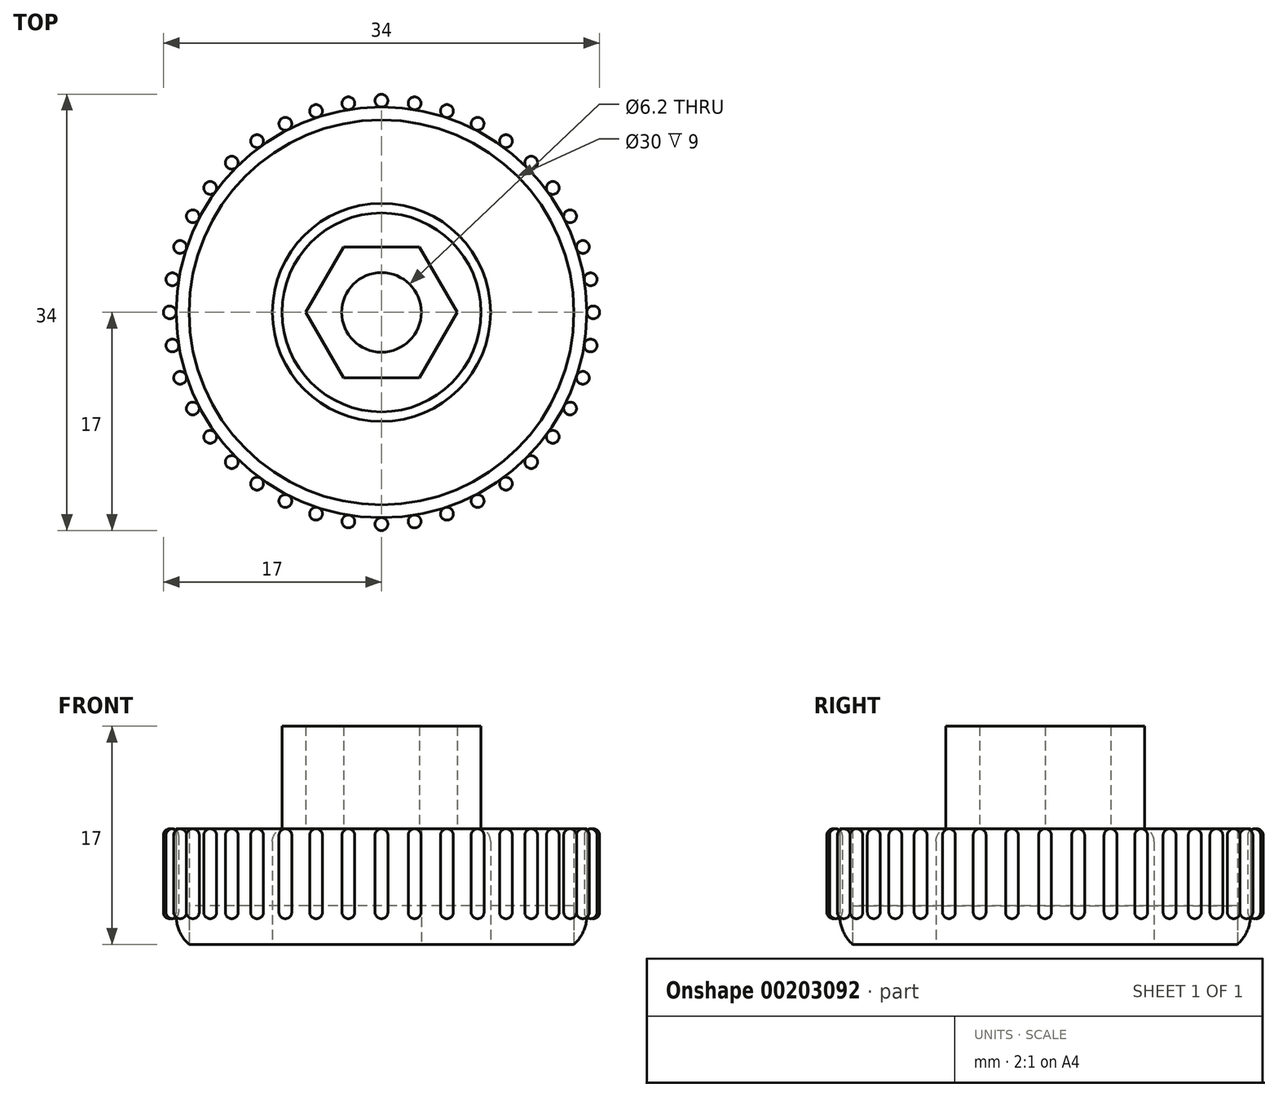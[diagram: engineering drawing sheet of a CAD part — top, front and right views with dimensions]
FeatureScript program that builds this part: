
annotation { "Feature Type Name" : "Feature", "Feature Type Description" : "" }
export const myFeature = defineFeature(function(context is Context, id is Id, definition is map)
    precondition{}
    {
        {
            var Q0;
            Q0=qCreatedBy(makeId("Top.planeOp"),FACE);
            var sketch = newSketch(context, id + "F0", { "sketchPlane" : qUnion([Q0])});
            skCircle(sketch, "E0.cCircle", {"center": v(0, 0) * mm, "radius": 5.9 * mm, "construction": true});
            skLineSegment(sketch, "E0.0", {"start": v(5.9, 0) * mm, "end": v(2.95, -5.1) * mm});
            skLineSegment(sketch, "E0.1", {"start": v(2.95, -5.1) * mm, "end": v(-2.95, -5.1) * mm});
            skLineSegment(sketch, "E0.2", {"start": v(-2.95, -5.1) * mm, "end": v(-5.9, 0) * mm});
            skLineSegment(sketch, "E0.3", {"start": v(-5.9, 0) * mm, "end": v(-2.95, 5.1) * mm});
            skLineSegment(sketch, "E0.4", {"start": v(-2.95, 5.1) * mm, "end": v(2.95, 5.1) * mm});
            skLineSegment(sketch, "E0.5", {"start": v(2.95, 5.1) * mm, "end": v(5.9, 0) * mm});
            skCircle(sketch, "E1", {"center": v(0, 0) * mm, "radius": 7.75 * mm});
            skCircle(sketch, "E2", {"center": v(0, 0) * mm, "radius": 8.5 * mm});
            skCircle(sketch, "E3", {"center": v(0, 0) * mm, "radius": 16 * mm});
            skCircle(sketch, "E4", {"center": v(0, 0) * mm, "radius": 15 * mm});
            skCircle(sketch, "E5", {"center": v(0, 0) * mm, "radius": 3.1 * mm});
            skSolve(sketch);
        }
        {
            var Q0;
            Q0=qCreatedBy(makeId("Top.planeOp"),FACE);
            var sketch = newSketch(context, id + "F1", { "sketchPlane" : qUnion([Q0])});
            skCircle(sketch, "E6", {"center": v(0, 16.5) * mm, "radius": 0.5 * mm});
            skCircle(sketch, "E7.1.0", {"center": v(-2.58, 16.3) * mm, "radius": 0.5 * mm});
            skCircle(sketch, "E7.2.0", {"center": v(-5.1, 15.7) * mm, "radius": 0.5 * mm});
            skCircle(sketch, "E7.3.0", {"center": v(-7.5, 14.7) * mm, "radius": 0.5 * mm});
            skCircle(sketch, "E7.4.0", {"center": v(-9.7, 13.35) * mm, "radius": 0.5 * mm});
            skCircle(sketch, "E7.5.0", {"center": v(-11.67, 11.67) * mm, "radius": 0.5 * mm});
            skCircle(sketch, "E7.6.0", {"center": v(-13.35, 9.7) * mm, "radius": 0.5 * mm});
            skCircle(sketch, "E7.7.0", {"center": v(-14.7, 7.5) * mm, "radius": 0.5 * mm});
            skCircle(sketch, "E7.8.0", {"center": v(-15.7, 5.1) * mm, "radius": 0.5 * mm});
            skCircle(sketch, "E7.9.0", {"center": v(-16.3, 2.58) * mm, "radius": 0.5 * mm});
            skCircle(sketch, "E7.10.0", {"center": v(-16.5, 0) * mm, "radius": 0.5 * mm});
            skCircle(sketch, "E7.11.0", {"center": v(-16.3, -2.58) * mm, "radius": 0.5 * mm});
            skCircle(sketch, "E7.12.0", {"center": v(-15.7, -5.1) * mm, "radius": 0.5 * mm});
            skCircle(sketch, "E7.13.0", {"center": v(-14.7, -7.5) * mm, "radius": 0.5 * mm});
            skCircle(sketch, "E7.14.0", {"center": v(-13.35, -9.7) * mm, "radius": 0.5 * mm});
            skCircle(sketch, "E7.15.0", {"center": v(-11.67, -11.67) * mm, "radius": 0.5 * mm});
            skCircle(sketch, "E7.16.0", {"center": v(-9.7, -13.35) * mm, "radius": 0.5 * mm});
            skCircle(sketch, "E7.17.0", {"center": v(-7.5, -14.7) * mm, "radius": 0.5 * mm});
            skCircle(sketch, "E7.18.0", {"center": v(-5.1, -15.7) * mm, "radius": 0.5 * mm});
            skCircle(sketch, "E7.19.0", {"center": v(-2.58, -16.3) * mm, "radius": 0.5 * mm});
            skCircle(sketch, "E7.20.0", {"center": v(0, -16.5) * mm, "radius": 0.5 * mm});
            skCircle(sketch, "E7.21.0", {"center": v(2.58, -16.3) * mm, "radius": 0.5 * mm});
            skCircle(sketch, "E7.22.0", {"center": v(5.1, -15.7) * mm, "radius": 0.5 * mm});
            skCircle(sketch, "E7.23.0", {"center": v(7.5, -14.7) * mm, "radius": 0.5 * mm});
            skCircle(sketch, "E7.24.0", {"center": v(9.7, -13.35) * mm, "radius": 0.5 * mm});
            skCircle(sketch, "E7.25.0", {"center": v(11.67, -11.67) * mm, "radius": 0.5 * mm});
            skCircle(sketch, "E7.26.0", {"center": v(13.35, -9.7) * mm, "radius": 0.5 * mm});
            skCircle(sketch, "E7.27.0", {"center": v(14.7, -7.5) * mm, "radius": 0.5 * mm});
            skCircle(sketch, "E7.28.0", {"center": v(15.7, -5.1) * mm, "radius": 0.5 * mm});
            skCircle(sketch, "E7.29.0", {"center": v(16.3, -2.58) * mm, "radius": 0.5 * mm});
            skCircle(sketch, "E7.30.0", {"center": v(16.5, 0) * mm, "radius": 0.5 * mm});
            skCircle(sketch, "E7.31.0", {"center": v(16.3, 2.58) * mm, "radius": 0.5 * mm});
            skCircle(sketch, "E7.32.0", {"center": v(15.7, 5.1) * mm, "radius": 0.5 * mm});
            skCircle(sketch, "E7.33.0", {"center": v(14.7, 7.5) * mm, "radius": 0.5 * mm});
            skCircle(sketch, "E7.34.0", {"center": v(13.35, 9.7) * mm, "radius": 0.5 * mm});
            skCircle(sketch, "E7.35.0", {"center": v(11.67, 11.67) * mm, "radius": 0.5 * mm});
            skCircle(sketch, "E7.36.0", {"center": v(9.7, 13.35) * mm, "radius": 0.5 * mm});
            skCircle(sketch, "E7.37.0", {"center": v(7.5, 14.7) * mm, "radius": 0.5 * mm});
            skCircle(sketch, "E7.38.0", {"center": v(5.1, 15.7) * mm, "radius": 0.5 * mm});
            skCircle(sketch, "E7.39.0", {"center": v(2.58, 16.3) * mm, "radius": 0.5 * mm});
            skPoint(sketch, "E7.center", {"position": v(0, 0) * mm});
            skSolve(sketch);
        }
        {
            var Q0;
            Q0=makeQuery(id+"F1.imprint","IMPRINT",FACE,{"disambiguationData":[TD([[makeQuery(id+"F1.imprint","IMPRINT",EDGE,{"derivedFrom":sQuery(id+"F1.wireOp",EDGE,"E6")}),1.0]])]});
            var Q1;
            Q1=makeQuery(id+"F1.imprint","IMPRINT",FACE,{"disambiguationData":[TD([[makeQuery(id+"F1.imprint","IMPRINT",EDGE,{"derivedFrom":sQuery(id+"F1.wireOp",EDGE,"E7.39.0")}),1.0]])]});
            var Q2;
            Q2=makeQuery(id+"F1.imprint","IMPRINT",FACE,{"disambiguationData":[TD([[makeQuery(id+"F1.imprint","IMPRINT",EDGE,{"derivedFrom":sQuery(id+"F1.wireOp",EDGE,"E7.38.0")}),1.0]])]});
            var Q3;
            Q3=makeQuery(id+"F1.imprint","IMPRINT",FACE,{"disambiguationData":[TD([[makeQuery(id+"F1.imprint","IMPRINT",EDGE,{"derivedFrom":sQuery(id+"F1.wireOp",EDGE,"E7.37.0")}),1.0]])]});
            var Q4;
            Q4=makeQuery(id+"F1.imprint","IMPRINT",FACE,{"disambiguationData":[TD([[makeQuery(id+"F1.imprint","IMPRINT",EDGE,{"derivedFrom":sQuery(id+"F1.wireOp",EDGE,"E7.36.0")}),1.0]])]});
            var Q5;
            Q5=makeQuery(id+"F1.imprint","IMPRINT",FACE,{"disambiguationData":[TD([[makeQuery(id+"F1.imprint","IMPRINT",EDGE,{"derivedFrom":sQuery(id+"F1.wireOp",EDGE,"E7.35.0")}),1.0]])]});
            var Q6;
            Q6=makeQuery(id+"F1.imprint","IMPRINT",FACE,{"disambiguationData":[TD([[makeQuery(id+"F1.imprint","IMPRINT",EDGE,{"derivedFrom":sQuery(id+"F1.wireOp",EDGE,"E7.1.0")}),1.0]])]});
            var Q7;
            Q7=makeQuery(id+"F1.imprint","IMPRINT",FACE,{"disambiguationData":[TD([[makeQuery(id+"F1.imprint","IMPRINT",EDGE,{"derivedFrom":sQuery(id+"F1.wireOp",EDGE,"E7.2.0")}),1.0]])]});
            var Q8;
            Q8=makeQuery(id+"F1.imprint","IMPRINT",FACE,{"disambiguationData":[TD([[makeQuery(id+"F1.imprint","IMPRINT",EDGE,{"derivedFrom":sQuery(id+"F1.wireOp",EDGE,"E7.3.0")}),1.0]])]});
            var Q9;
            Q9=makeQuery(id+"F1.imprint","IMPRINT",FACE,{"disambiguationData":[TD([[makeQuery(id+"F1.imprint","IMPRINT",EDGE,{"derivedFrom":sQuery(id+"F1.wireOp",EDGE,"E7.4.0")}),1.0]])]});
            var Q10;
            Q10=makeQuery(id+"F1.imprint","IMPRINT",FACE,{"disambiguationData":[TD([[makeQuery(id+"F1.imprint","IMPRINT",EDGE,{"derivedFrom":sQuery(id+"F1.wireOp",EDGE,"E7.5.0")}),1.0]])]});
            var Q11;
            Q11=makeQuery(id+"F1.imprint","IMPRINT",FACE,{"disambiguationData":[TD([[makeQuery(id+"F1.imprint","IMPRINT",EDGE,{"derivedFrom":sQuery(id+"F1.wireOp",EDGE,"E7.6.0")}),1.0]])]});
            var Q12;
            Q12=makeQuery(id+"F1.imprint","IMPRINT",FACE,{"disambiguationData":[TD([[makeQuery(id+"F1.imprint","IMPRINT",EDGE,{"derivedFrom":sQuery(id+"F1.wireOp",EDGE,"E7.7.0")}),1.0]])]});
            var Q13;
            Q13=makeQuery(id+"F1.imprint","IMPRINT",FACE,{"disambiguationData":[TD([[makeQuery(id+"F1.imprint","IMPRINT",EDGE,{"derivedFrom":sQuery(id+"F1.wireOp",EDGE,"E7.8.0")}),1.0]])]});
            var Q14;
            Q14=makeQuery(id+"F1.imprint","IMPRINT",FACE,{"disambiguationData":[TD([[makeQuery(id+"F1.imprint","IMPRINT",EDGE,{"derivedFrom":sQuery(id+"F1.wireOp",EDGE,"E7.9.0")}),1.0]])]});
            var Q15;
            Q15=makeQuery(id+"F1.imprint","IMPRINT",FACE,{"disambiguationData":[TD([[makeQuery(id+"F1.imprint","IMPRINT",EDGE,{"derivedFrom":sQuery(id+"F1.wireOp",EDGE,"E7.10.0")}),1.0]])]});
            var Q16;
            Q16=makeQuery(id+"F1.imprint","IMPRINT",FACE,{"disambiguationData":[TD([[makeQuery(id+"F1.imprint","IMPRINT",EDGE,{"derivedFrom":sQuery(id+"F1.wireOp",EDGE,"E7.11.0")}),1.0]])]});
            var Q17;
            Q17=makeQuery(id+"F1.imprint","IMPRINT",FACE,{"disambiguationData":[TD([[makeQuery(id+"F1.imprint","IMPRINT",EDGE,{"derivedFrom":sQuery(id+"F1.wireOp",EDGE,"E7.12.0")}),1.0]])]});
            var Q18;
            Q18=makeQuery(id+"F1.imprint","IMPRINT",FACE,{"disambiguationData":[TD([[makeQuery(id+"F1.imprint","IMPRINT",EDGE,{"derivedFrom":sQuery(id+"F1.wireOp",EDGE,"E7.13.0")}),1.0]])]});
            var Q19;
            Q19=makeQuery(id+"F1.imprint","IMPRINT",FACE,{"disambiguationData":[TD([[makeQuery(id+"F1.imprint","IMPRINT",EDGE,{"derivedFrom":sQuery(id+"F1.wireOp",EDGE,"E7.14.0")}),1.0]])]});
            var Q20;
            Q20=makeQuery(id+"F1.imprint","IMPRINT",FACE,{"disambiguationData":[TD([[makeQuery(id+"F1.imprint","IMPRINT",EDGE,{"derivedFrom":sQuery(id+"F1.wireOp",EDGE,"E7.15.0")}),1.0]])]});
            var Q21;
            Q21=makeQuery(id+"F1.imprint","IMPRINT",FACE,{"disambiguationData":[TD([[makeQuery(id+"F1.imprint","IMPRINT",EDGE,{"derivedFrom":sQuery(id+"F1.wireOp",EDGE,"E7.16.0")}),1.0]])]});
            var Q22;
            Q22=makeQuery(id+"F1.imprint","IMPRINT",FACE,{"disambiguationData":[TD([[makeQuery(id+"F1.imprint","IMPRINT",EDGE,{"derivedFrom":sQuery(id+"F1.wireOp",EDGE,"E7.17.0")}),1.0]])]});
            var Q23;
            Q23=makeQuery(id+"F1.imprint","IMPRINT",FACE,{"disambiguationData":[TD([[makeQuery(id+"F1.imprint","IMPRINT",EDGE,{"derivedFrom":sQuery(id+"F1.wireOp",EDGE,"E7.18.0")}),1.0]])]});
            var Q24;
            Q24=makeQuery(id+"F1.imprint","IMPRINT",FACE,{"disambiguationData":[TD([[makeQuery(id+"F1.imprint","IMPRINT",EDGE,{"derivedFrom":sQuery(id+"F1.wireOp",EDGE,"E7.19.0")}),1.0]])]});
            var Q25;
            Q25=makeQuery(id+"F1.imprint","IMPRINT",FACE,{"disambiguationData":[TD([[makeQuery(id+"F1.imprint","IMPRINT",EDGE,{"derivedFrom":sQuery(id+"F1.wireOp",EDGE,"E7.20.0")}),1.0]])]});
            var Q26;
            Q26=makeQuery(id+"F1.imprint","IMPRINT",FACE,{"disambiguationData":[TD([[makeQuery(id+"F1.imprint","IMPRINT",EDGE,{"derivedFrom":sQuery(id+"F1.wireOp",EDGE,"E7.21.0")}),1.0]])]});
            var Q27;
            Q27=makeQuery(id+"F1.imprint","IMPRINT",FACE,{"disambiguationData":[TD([[makeQuery(id+"F1.imprint","IMPRINT",EDGE,{"derivedFrom":sQuery(id+"F1.wireOp",EDGE,"E7.22.0")}),1.0]])]});
            var Q28;
            Q28=makeQuery(id+"F1.imprint","IMPRINT",FACE,{"disambiguationData":[TD([[makeQuery(id+"F1.imprint","IMPRINT",EDGE,{"derivedFrom":sQuery(id+"F1.wireOp",EDGE,"E7.23.0")}),1.0]])]});
            var Q29;
            Q29=makeQuery(id+"F1.imprint","IMPRINT",FACE,{"disambiguationData":[TD([[makeQuery(id+"F1.imprint","IMPRINT",EDGE,{"derivedFrom":sQuery(id+"F1.wireOp",EDGE,"E7.24.0")}),1.0]])]});
            var Q30;
            Q30=makeQuery(id+"F1.imprint","IMPRINT",FACE,{"disambiguationData":[TD([[makeQuery(id+"F1.imprint","IMPRINT",EDGE,{"derivedFrom":sQuery(id+"F1.wireOp",EDGE,"E7.25.0")}),1.0]])]});
            var Q31;
            Q31=makeQuery(id+"F1.imprint","IMPRINT",FACE,{"disambiguationData":[TD([[makeQuery(id+"F1.imprint","IMPRINT",EDGE,{"derivedFrom":sQuery(id+"F1.wireOp",EDGE,"E7.26.0")}),1.0]])]});
            var Q32;
            Q32=makeQuery(id+"F1.imprint","IMPRINT",FACE,{"disambiguationData":[TD([[makeQuery(id+"F1.imprint","IMPRINT",EDGE,{"derivedFrom":sQuery(id+"F1.wireOp",EDGE,"E7.27.0")}),1.0]])]});
            var Q33;
            Q33=makeQuery(id+"F1.imprint","IMPRINT",FACE,{"disambiguationData":[TD([[makeQuery(id+"F1.imprint","IMPRINT",EDGE,{"derivedFrom":sQuery(id+"F1.wireOp",EDGE,"E7.28.0")}),1.0]])]});
            var Q34;
            Q34=makeQuery(id+"F1.imprint","IMPRINT",FACE,{"disambiguationData":[TD([[makeQuery(id+"F1.imprint","IMPRINT",EDGE,{"derivedFrom":sQuery(id+"F1.wireOp",EDGE,"E7.29.0")}),1.0]])]});
            var Q35;
            Q35=makeQuery(id+"F1.imprint","IMPRINT",FACE,{"disambiguationData":[TD([[makeQuery(id+"F1.imprint","IMPRINT",EDGE,{"derivedFrom":sQuery(id+"F1.wireOp",EDGE,"E7.34.0")}),1.0]])]});
            var Q36;
            Q36=makeQuery(id+"F1.imprint","IMPRINT",FACE,{"disambiguationData":[TD([[makeQuery(id+"F1.imprint","IMPRINT",EDGE,{"derivedFrom":sQuery(id+"F1.wireOp",EDGE,"E7.33.0")}),1.0]])]});
            var Q37;
            Q37=makeQuery(id+"F1.imprint","IMPRINT",FACE,{"disambiguationData":[TD([[makeQuery(id+"F1.imprint","IMPRINT",EDGE,{"derivedFrom":sQuery(id+"F1.wireOp",EDGE,"E7.32.0")}),1.0]])]});
            var Q38;
            Q38=makeQuery(id+"F1.imprint","IMPRINT",FACE,{"disambiguationData":[TD([[makeQuery(id+"F1.imprint","IMPRINT",EDGE,{"derivedFrom":sQuery(id+"F1.wireOp",EDGE,"E7.31.0")}),1.0]])]});
            var Q39;
            Q39=makeQuery(id+"F1.imprint","IMPRINT",FACE,{"disambiguationData":[TD([[makeQuery(id+"F1.imprint","IMPRINT",EDGE,{"derivedFrom":sQuery(id+"F1.wireOp",EDGE,"E7.30.0")}),1.0]])]});
            extrude(context, id + "F2", {"entities" : qUnion([Q0, Q1, Q2, Q3, Q4, Q5, Q6, Q7, Q8, Q9, Q10, Q11, Q12, Q13, Q14, Q15, Q16, Q17, Q18, Q19, Q20, Q21, Q22, Q23, Q24, Q25, Q26, Q27, Q28, Q29, Q30, Q31, Q32, Q33, Q34, Q35, Q36, Q37, Q38, Q39]), "depth" : 7 * mm});
        }
        {
            var Q0;
            Q0=makeQuery(id+"F0.imprint","IMPRINT",FACE,{"disambiguationData":[TD([[makeQuery(id+"F0.imprint","IMPRINT",EDGE,{"derivedFrom":sQuery(id+"F0.wireOp",EDGE,"E3")}),1.0]])]});
            var Q1;
            Q1=makeQuery(id+"F0.imprint","IMPRINT",FACE,{"disambiguationData":[TD([[makeQuery(id+"F0.imprint","IMPRINT",EDGE,{"derivedFrom":sQuery(id+"F0.wireOp",EDGE,"E1")}),-1.0]])]});
            var Q2;
            Q2=makeQuery(id+"F0.imprint","IMPRINT",FACE,{"disambiguationData":[TD([[makeQuery(id+"F0.imprint","IMPRINT",EDGE,{"derivedFrom":sQuery(id+"F0.wireOp",EDGE,"E0.0")}),-1.0]])]});
            extrude(context, id + "F3", {"entities" : qUnion([Q0, Q1, Q2]), "depth" : 9 * mm});
        }
        {
            var Q0;
            Q0=makeQuery(id+"F0.imprint","IMPRINT",FACE,{"disambiguationData":[TD([[makeQuery(id+"F0.imprint","IMPRINT",EDGE,{"derivedFrom":sQuery(id+"F0.wireOp",EDGE,"E0.0")}),1.0]])]});
            extrude(context, id + "F4", {"entities" : qUnion([Q0]), "operationType" : NewBodyOperationType.ADD, "depth" : 17 * mm});
        }
        {
            var Q0;
            Q0=makeQuery(id+"F2.opExtrude","SWEPT_BODY",BODY,{"disambiguationData":[OSD([sQuery(id+"F1.wireOp",EDGE,"E7.3.0")])]});
            var Q1;
            Q1=makeQuery(id+"F2.opExtrude","SWEPT_BODY",BODY,{"disambiguationData":[OSD([sQuery(id+"F1.wireOp",EDGE,"E7.2.0")])]});
            var Q2;
            Q2=makeQuery(id+"F2.opExtrude","SWEPT_BODY",BODY,{"disambiguationData":[OSD([sQuery(id+"F1.wireOp",EDGE,"E7.1.0")])]});
            var Q3;
            Q3=makeQuery(id+"F2.opExtrude","SWEPT_BODY",BODY,{"disambiguationData":[OSD([sQuery(id+"F1.wireOp",EDGE,"E6")])]});
            var Q4;
            Q4=makeQuery(id+"F2.opExtrude","SWEPT_BODY",BODY,{"disambiguationData":[OSD([sQuery(id+"F1.wireOp",EDGE,"E7.39.0")])]});
            var Q5;
            Q5=makeQuery(id+"F2.opExtrude","SWEPT_BODY",BODY,{"disambiguationData":[OSD([sQuery(id+"F1.wireOp",EDGE,"E7.38.0")])]});
            var Q6;
            Q6=makeQuery(id+"F2.opExtrude","SWEPT_BODY",BODY,{"disambiguationData":[OSD([sQuery(id+"F1.wireOp",EDGE,"E7.37.0")])]});
            var Q7;
            Q7=makeQuery(id+"F2.opExtrude","SWEPT_BODY",BODY,{"disambiguationData":[OSD([sQuery(id+"F1.wireOp",EDGE,"E7.36.0")])]});
            var Q8;
            Q8=makeQuery(id+"F2.opExtrude","SWEPT_BODY",BODY,{"disambiguationData":[OSD([sQuery(id+"F1.wireOp",EDGE,"E7.35.0")])]});
            var Q9;
            Q9=makeQuery(id+"F2.opExtrude","SWEPT_BODY",BODY,{"disambiguationData":[OSD([sQuery(id+"F1.wireOp",EDGE,"E7.34.0")])]});
            var Q10;
            Q10=makeQuery(id+"F2.opExtrude","SWEPT_BODY",BODY,{"disambiguationData":[OSD([sQuery(id+"F1.wireOp",EDGE,"E7.33.0")])]});
            var Q11;
            Q11=makeQuery(id+"F2.opExtrude","SWEPT_BODY",BODY,{"disambiguationData":[OSD([sQuery(id+"F1.wireOp",EDGE,"E7.4.0")])]});
            var Q12;
            Q12=makeQuery(id+"F2.opExtrude","SWEPT_BODY",BODY,{"disambiguationData":[OSD([sQuery(id+"F1.wireOp",EDGE,"E7.5.0")])]});
            var Q13;
            Q13=makeQuery(id+"F2.opExtrude","SWEPT_BODY",BODY,{"disambiguationData":[OSD([sQuery(id+"F1.wireOp",EDGE,"E7.6.0")])]});
            var Q14;
            Q14=makeQuery(id+"F2.opExtrude","SWEPT_BODY",BODY,{"disambiguationData":[OSD([sQuery(id+"F1.wireOp",EDGE,"E7.7.0")])]});
            var Q15;
            Q15=makeQuery(id+"F2.opExtrude","SWEPT_BODY",BODY,{"disambiguationData":[OSD([sQuery(id+"F1.wireOp",EDGE,"E7.8.0")])]});
            var Q16;
            Q16=makeQuery(id+"F2.opExtrude","SWEPT_BODY",BODY,{"disambiguationData":[OSD([sQuery(id+"F1.wireOp",EDGE,"E7.9.0")])]});
            var Q17;
            Q17=makeQuery(id+"F2.opExtrude","SWEPT_BODY",BODY,{"disambiguationData":[OSD([sQuery(id+"F1.wireOp",EDGE,"E7.31.0")])]});
            var Q18;
            Q18=makeQuery(id+"F2.opExtrude","SWEPT_BODY",BODY,{"disambiguationData":[OSD([sQuery(id+"F1.wireOp",EDGE,"E7.30.0")])]});
            var Q19;
            Q19=makeQuery(id+"F2.opExtrude","SWEPT_BODY",BODY,{"disambiguationData":[OSD([sQuery(id+"F1.wireOp",EDGE,"E7.28.0")])]});
            var Q20;
            Q20=makeQuery(id+"F2.opExtrude","SWEPT_BODY",BODY,{"disambiguationData":[OSD([sQuery(id+"F1.wireOp",EDGE,"E7.27.0")])]});
            var Q21;
            Q21=makeQuery(id+"F2.opExtrude","SWEPT_BODY",BODY,{"disambiguationData":[OSD([sQuery(id+"F1.wireOp",EDGE,"E7.26.0")])]});
            var Q22;
            Q22=makeQuery(id+"F2.opExtrude","SWEPT_BODY",BODY,{"disambiguationData":[OSD([sQuery(id+"F1.wireOp",EDGE,"E7.25.0")])]});
            var Q23;
            Q23=makeQuery(id+"F2.opExtrude","SWEPT_BODY",BODY,{"disambiguationData":[OSD([sQuery(id+"F1.wireOp",EDGE,"E7.24.0")])]});
            var Q24;
            Q24=makeQuery(id+"F2.opExtrude","SWEPT_BODY",BODY,{"disambiguationData":[OSD([sQuery(id+"F1.wireOp",EDGE,"E7.23.0")])]});
            var Q25;
            Q25=makeQuery(id+"F2.opExtrude","SWEPT_BODY",BODY,{"disambiguationData":[OSD([sQuery(id+"F1.wireOp",EDGE,"E7.22.0")])]});
            var Q26;
            Q26=makeQuery(id+"F2.opExtrude","SWEPT_BODY",BODY,{"disambiguationData":[OSD([sQuery(id+"F1.wireOp",EDGE,"E7.21.0")])]});
            var Q27;
            Q27=makeQuery(id+"F2.opExtrude","SWEPT_BODY",BODY,{"disambiguationData":[OSD([sQuery(id+"F1.wireOp",EDGE,"E7.20.0")])]});
            var Q28;
            Q28=makeQuery(id+"F2.opExtrude","SWEPT_BODY",BODY,{"disambiguationData":[OSD([sQuery(id+"F1.wireOp",EDGE,"E7.19.0")])]});
            var Q29;
            Q29=makeQuery(id+"F2.opExtrude","SWEPT_BODY",BODY,{"disambiguationData":[OSD([sQuery(id+"F1.wireOp",EDGE,"E7.18.0")])]});
            var Q30;
            Q30=makeQuery(id+"F2.opExtrude","SWEPT_BODY",BODY,{"disambiguationData":[OSD([sQuery(id+"F1.wireOp",EDGE,"E7.17.0")])]});
            var Q31;
            Q31=makeQuery(id+"F2.opExtrude","SWEPT_BODY",BODY,{"disambiguationData":[OSD([sQuery(id+"F1.wireOp",EDGE,"E7.16.0")])]});
            var Q32;
            Q32=makeQuery(id+"F2.opExtrude","SWEPT_BODY",BODY,{"disambiguationData":[OSD([sQuery(id+"F1.wireOp",EDGE,"E7.15.0")])]});
            var Q33;
            Q33=makeQuery(id+"F2.opExtrude","SWEPT_BODY",BODY,{"disambiguationData":[OSD([sQuery(id+"F1.wireOp",EDGE,"E7.14.0")])]});
            var Q34;
            Q34=makeQuery(id+"F2.opExtrude","SWEPT_BODY",BODY,{"disambiguationData":[OSD([sQuery(id+"F1.wireOp",EDGE,"E7.10.0")])]});
            var Q35;
            Q35=makeQuery(id+"F2.opExtrude","SWEPT_BODY",BODY,{"disambiguationData":[OSD([sQuery(id+"F1.wireOp",EDGE,"E7.11.0")])]});
            var Q36;
            Q36=makeQuery(id+"F2.opExtrude","SWEPT_BODY",BODY,{"disambiguationData":[OSD([sQuery(id+"F1.wireOp",EDGE,"E7.12.0")])]});
            var Q37;
            Q37=makeQuery(id+"F2.opExtrude","SWEPT_BODY",BODY,{"disambiguationData":[OSD([sQuery(id+"F1.wireOp",EDGE,"E7.13.0")])]});
            var Q38;
            Q38=makeQuery(id+"F2.opExtrude","SWEPT_BODY",BODY,{"disambiguationData":[OSD([sQuery(id+"F1.wireOp",EDGE,"E7.32.0")])]});
            var Q39;
            Q39=makeQuery(id+"F2.opExtrude","SWEPT_BODY",BODY,{"disambiguationData":[OSD([sQuery(id+"F1.wireOp",EDGE,"E7.29.0")])]});
            transform(context, id + "F5", {"entities" : qUnion([Q0, Q1, Q2, Q3, Q4, Q5, Q6, Q7, Q8, Q9, Q10, Q11, Q12, Q13, Q14, Q15, Q16, Q17, Q18, Q19, Q20, Q21, Q22, Q23, Q24, Q25, Q26, Q27, Q28, Q29, Q30, Q31, Q32, Q33, Q34, Q35, Q36, Q37, Q38, Q39]), "transformType" : TransformType.TRANSLATION_3D, "dx" : 0 * mm, "dy" : 0 * mm, "dz" : 2 * mm, "makeCopy" : false});
        }
        {
            var Q0;
            Q0=makeQuery(id+"F2.opExtrude","SWEPT_FACE",FACE,{"disambiguationData":[OSD([sQuery(id+"F1.wireOp",EDGE,"E7.24.0")])]});
            var Q1;
            Q1=makeQuery(id+"F2.opExtrude","SWEPT_FACE",FACE,{"disambiguationData":[OSD([sQuery(id+"F1.wireOp",EDGE,"E7.25.0")])]});
            var Q2;
            Q2=makeQuery(id+"F2.opExtrude","SWEPT_FACE",FACE,{"disambiguationData":[OSD([sQuery(id+"F1.wireOp",EDGE,"E7.27.0")])]});
            var Q3;
            Q3=makeQuery(id+"F2.opExtrude","SWEPT_FACE",FACE,{"disambiguationData":[OSD([sQuery(id+"F1.wireOp",EDGE,"E7.28.0")])]});
            var Q4;
            Q4=makeQuery(id+"F2.opExtrude","SWEPT_FACE",FACE,{"disambiguationData":[OSD([sQuery(id+"F1.wireOp",EDGE,"E7.29.0")])]});
            var Q5;
            Q5=makeQuery(id+"F2.opExtrude","SWEPT_FACE",FACE,{"disambiguationData":[OSD([sQuery(id+"F1.wireOp",EDGE,"E7.30.0")])]});
            var Q6;
            Q6=makeQuery(id+"F2.opExtrude","SWEPT_FACE",FACE,{"disambiguationData":[OSD([sQuery(id+"F1.wireOp",EDGE,"E7.31.0")])]});
            var Q7;
            Q7=makeQuery(id+"F2.opExtrude","SWEPT_FACE",FACE,{"disambiguationData":[OSD([sQuery(id+"F1.wireOp",EDGE,"E7.32.0")])]});
            var Q8;
            Q8=makeQuery(id+"F2.opExtrude","SWEPT_FACE",FACE,{"disambiguationData":[OSD([sQuery(id+"F1.wireOp",EDGE,"E7.33.0")])]});
            var Q9;
            Q9=makeQuery(id+"F2.opExtrude","SWEPT_FACE",FACE,{"disambiguationData":[OSD([sQuery(id+"F1.wireOp",EDGE,"E7.34.0")])]});
            var Q10;
            Q10=makeQuery(id+"F2.opExtrude","SWEPT_FACE",FACE,{"disambiguationData":[OSD([sQuery(id+"F1.wireOp",EDGE,"E7.35.0")])]});
            var Q11;
            Q11=makeQuery(id+"F2.opExtrude","SWEPT_FACE",FACE,{"disambiguationData":[OSD([sQuery(id+"F1.wireOp",EDGE,"E7.36.0")])]});
            var Q12;
            Q12=makeQuery(id+"F2.opExtrude","SWEPT_FACE",FACE,{"disambiguationData":[OSD([sQuery(id+"F1.wireOp",EDGE,"E7.37.0")])]});
            var Q13;
            Q13=makeQuery(id+"F2.opExtrude","SWEPT_FACE",FACE,{"disambiguationData":[OSD([sQuery(id+"F1.wireOp",EDGE,"E7.38.0")])]});
            var Q14;
            Q14=makeQuery(id+"F2.opExtrude","SWEPT_FACE",FACE,{"disambiguationData":[OSD([sQuery(id+"F1.wireOp",EDGE,"E7.39.0")])]});
            var Q15;
            Q15=makeQuery(id+"F2.opExtrude","SWEPT_FACE",FACE,{"disambiguationData":[OSD([sQuery(id+"F1.wireOp",EDGE,"E6")])]});
            var Q16;
            Q16=makeQuery(id+"F2.opExtrude","SWEPT_FACE",FACE,{"disambiguationData":[OSD([sQuery(id+"F1.wireOp",EDGE,"E7.1.0")])]});
            var Q17;
            Q17=makeQuery(id+"F2.opExtrude","SWEPT_FACE",FACE,{"disambiguationData":[OSD([sQuery(id+"F1.wireOp",EDGE,"E7.2.0")])]});
            var Q18;
            Q18=makeQuery(id+"F2.opExtrude","SWEPT_FACE",FACE,{"disambiguationData":[OSD([sQuery(id+"F1.wireOp",EDGE,"E7.3.0")])]});
            var Q19;
            Q19=makeQuery(id+"F2.opExtrude","SWEPT_FACE",FACE,{"disambiguationData":[OSD([sQuery(id+"F1.wireOp",EDGE,"E7.4.0")])]});
            var Q20;
            Q20=makeQuery(id+"F2.opExtrude","SWEPT_FACE",FACE,{"disambiguationData":[OSD([sQuery(id+"F1.wireOp",EDGE,"E7.5.0")])]});
            var Q21;
            Q21=makeQuery(id+"F2.opExtrude","SWEPT_FACE",FACE,{"disambiguationData":[OSD([sQuery(id+"F1.wireOp",EDGE,"E7.23.0")])]});
            var Q22;
            Q22=makeQuery(id+"F2.opExtrude","SWEPT_FACE",FACE,{"disambiguationData":[OSD([sQuery(id+"F1.wireOp",EDGE,"E7.22.0")])]});
            var Q23;
            Q23=makeQuery(id+"F2.opExtrude","SWEPT_FACE",FACE,{"disambiguationData":[OSD([sQuery(id+"F1.wireOp",EDGE,"E7.21.0")])]});
            var Q24;
            Q24=makeQuery(id+"F2.opExtrude","SWEPT_FACE",FACE,{"disambiguationData":[OSD([sQuery(id+"F1.wireOp",EDGE,"E7.20.0")])]});
            var Q25;
            Q25=makeQuery(id+"F2.opExtrude","SWEPT_FACE",FACE,{"disambiguationData":[OSD([sQuery(id+"F1.wireOp",EDGE,"E7.19.0")])]});
            var Q26;
            Q26=makeQuery(id+"F2.opExtrude","SWEPT_FACE",FACE,{"disambiguationData":[OSD([sQuery(id+"F1.wireOp",EDGE,"E7.18.0")])]});
            var Q27;
            Q27=makeQuery(id+"F2.opExtrude","SWEPT_FACE",FACE,{"disambiguationData":[OSD([sQuery(id+"F1.wireOp",EDGE,"E7.17.0")])]});
            var Q28;
            Q28=makeQuery(id+"F2.opExtrude","SWEPT_FACE",FACE,{"disambiguationData":[OSD([sQuery(id+"F1.wireOp",EDGE,"E7.16.0")])]});
            var Q29;
            Q29=makeQuery(id+"F2.opExtrude","SWEPT_FACE",FACE,{"disambiguationData":[OSD([sQuery(id+"F1.wireOp",EDGE,"E7.15.0")])]});
            var Q30;
            Q30=makeQuery(id+"F2.opExtrude","SWEPT_FACE",FACE,{"disambiguationData":[OSD([sQuery(id+"F1.wireOp",EDGE,"E7.14.0")])]});
            var Q31;
            Q31=makeQuery(id+"F2.opExtrude","SWEPT_FACE",FACE,{"disambiguationData":[OSD([sQuery(id+"F1.wireOp",EDGE,"E7.13.0")])]});
            var Q32;
            Q32=makeQuery(id+"F2.opExtrude","SWEPT_FACE",FACE,{"disambiguationData":[OSD([sQuery(id+"F1.wireOp",EDGE,"E7.12.0")])]});
            var Q33;
            Q33=makeQuery(id+"F2.opExtrude","SWEPT_FACE",FACE,{"disambiguationData":[OSD([sQuery(id+"F1.wireOp",EDGE,"E7.11.0")])]});
            var Q34;
            Q34=makeQuery(id+"F2.opExtrude","SWEPT_FACE",FACE,{"disambiguationData":[OSD([sQuery(id+"F1.wireOp",EDGE,"E7.10.0")])]});
            var Q35;
            Q35=makeQuery(id+"F2.opExtrude","SWEPT_FACE",FACE,{"disambiguationData":[OSD([sQuery(id+"F1.wireOp",EDGE,"E7.9.0")])]});
            var Q36;
            Q36=makeQuery(id+"F2.opExtrude","SWEPT_FACE",FACE,{"disambiguationData":[OSD([sQuery(id+"F1.wireOp",EDGE,"E7.8.0")])]});
            var Q37;
            Q37=makeQuery(id+"F2.opExtrude","SWEPT_FACE",FACE,{"disambiguationData":[OSD([sQuery(id+"F1.wireOp",EDGE,"E7.6.0")])]});
            var Q38;
            Q38=makeQuery(id+"F2.opExtrude","SWEPT_FACE",FACE,{"disambiguationData":[OSD([sQuery(id+"F1.wireOp",EDGE,"E7.7.0")])]});
            var Q39;
            Q39=makeQuery(id+"F2.opExtrude","SWEPT_FACE",FACE,{"disambiguationData":[OSD([sQuery(id+"F1.wireOp",EDGE,"E7.26.0")])]});
            fillet(context, id + "F6", {"entities" : qUnion([Q0, Q1, Q2, Q3, Q4, Q5, Q6, Q7, Q8, Q9, Q10, Q11, Q12, Q13, Q14, Q15, Q16, Q17, Q18, Q19, Q20, Q21, Q22, Q23, Q24, Q25, Q26, Q27, Q28, Q29, Q30, Q31, Q32, Q33, Q34, Q35, Q36, Q37, Q38, Q39]), "radius" : 0.5 * mm, "tangentPropagation" : true, "allowEdgeOverflow" : false});
        }
        {
            var Q0;
            Q0=makeQuery(id+"F3.opExtrude","CAP_EDGE",EDGE,{"disambiguationData":[OSD([sQuery(id+"F0.wireOp",EDGE,"E3")])],"isStart":true});
            fillet(context, id + "F7", {"entities" : qUnion([Q0]), "radius" : 3 * mm, "tangentPropagation" : true, "allowEdgeOverflow" : false});
        }
        {
            var Q0;
            Q0=makeQuery(id+"F3.opExtrude","CAP_EDGE",EDGE,{"disambiguationData":[OSD([sQuery(id+"F0.wireOp",EDGE,"E2")])],"isStart":false});
            fillet(context, id + "F8", {"entities" : qUnion([Q0]), "radius" : 1 * mm, "tangentPropagation" : true, "allowEdgeOverflow" : false});
        }
        {
            var Q0;
            Q0=makeQuery(id+"F0.imprint","IMPRINT",FACE,{"disambiguationData":[TD([[makeQuery(id+"F0.imprint","IMPRINT",EDGE,{"derivedFrom":sQuery(id+"F0.wireOp",EDGE,"E0.0")}),1.0]])]});
            var Q1;
            Q1=makeQuery(id+"F0.imprint","IMPRINT",FACE,{"disambiguationData":[TD([[makeQuery(id+"F0.imprint","IMPRINT",EDGE,{"derivedFrom":sQuery(id+"F0.wireOp",EDGE,"E2")}),-1.0]])]});
            var Q2;
            Q2=makeQuery(id+"F0.imprint","IMPRINT",FACE,{"disambiguationData":[TD([[makeQuery(id+"F0.imprint","IMPRINT",EDGE,{"derivedFrom":sQuery(id+"F0.wireOp",EDGE,"E0.0")}),-1.0]])]});
            var Q3;
            Q3=makeQuery(id+"F0.imprint","IMPRINT",FACE,{"disambiguationData":[TD([[makeQuery(id+"F0.imprint","IMPRINT",EDGE,{"derivedFrom":sQuery(id+"F0.wireOp",EDGE,"E5")}),1.0]])]});
            var Q4;
            Q4=makeQuery(id+"F0.imprint","IMPRINT",FACE,{"disambiguationData":[TD([[makeQuery(id+"F0.imprint","IMPRINT",EDGE,{"derivedFrom":sQuery(id+"F0.wireOp",EDGE,"E1")}),-1.0]])]});
            extrude(context, id + "F9", {"entities" : qUnion([Q0, Q1, Q2, Q3, Q4]), "depth" : 3 * mm});
        }
    });
